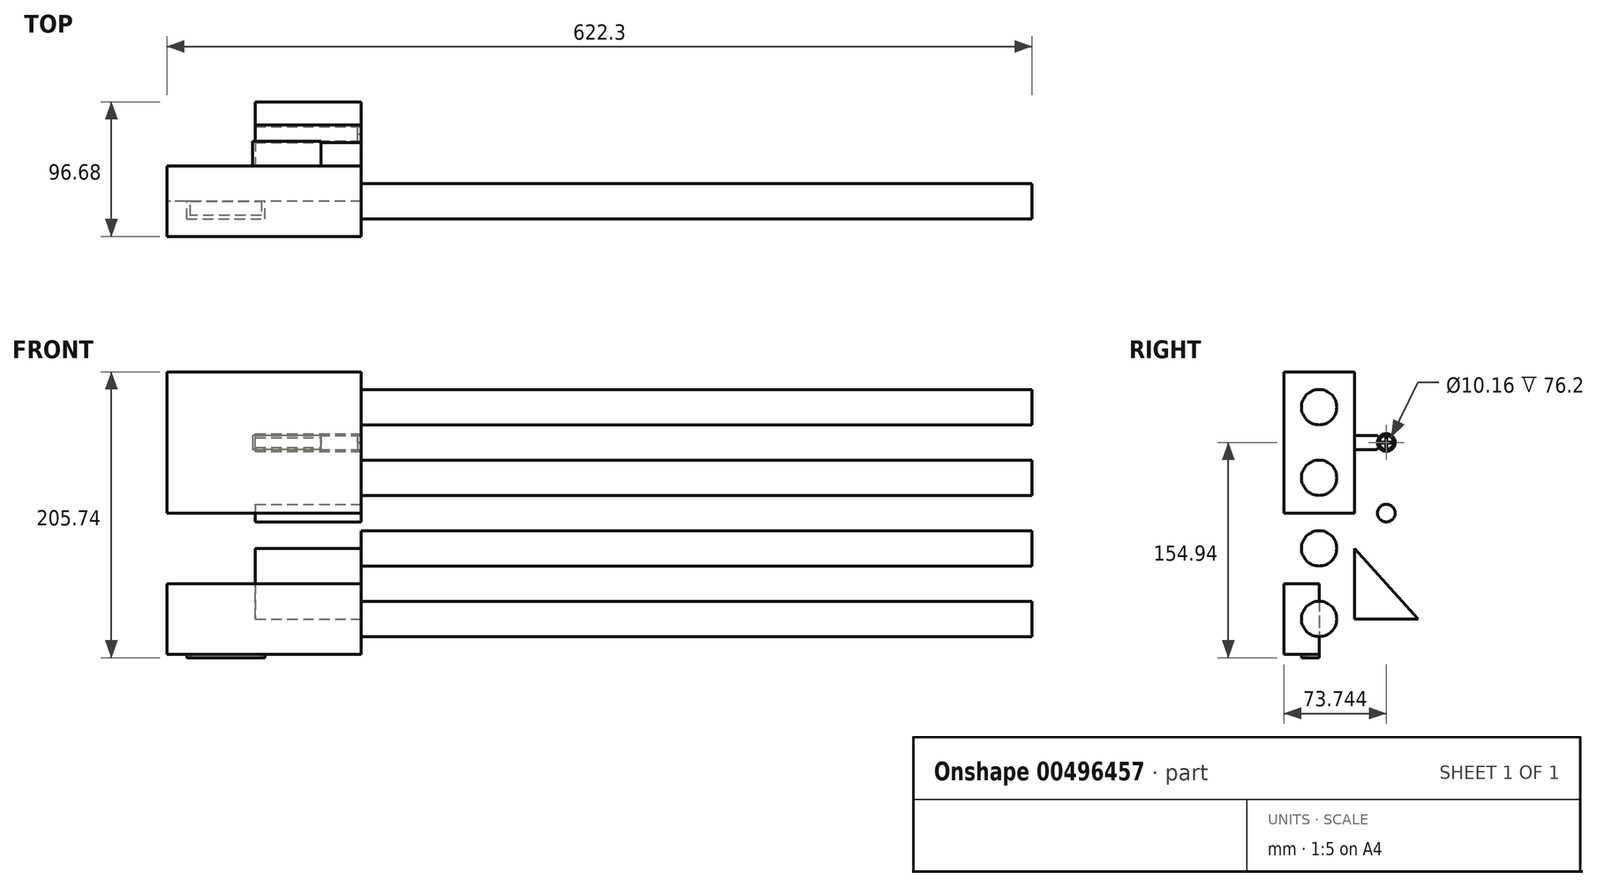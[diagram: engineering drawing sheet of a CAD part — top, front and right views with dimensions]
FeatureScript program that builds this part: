
annotation { "Feature Type Name" : "Feature", "Feature Type Description" : "" }
export const myFeature = defineFeature(function(context is Context, id is Id, definition is map)
    precondition{}
    {
        {
            var Q0;
            Q0=qCreatedBy(makeId("Top.planeOp"),FACE);
            var sketch = newSketch(context, id + "F0", { "sketchPlane" : qUnion([Q0])});
            skLineSegment(sketch, "E0.bottom", {"start": v(267.1, 70.34) * mm, "end": v(-139.3, 70.34) * mm});
            skLineSegment(sketch, "E0.top", {"start": v(267.1, 57.64) * mm, "end": v(-139.3, 57.64) * mm});
            skLineSegment(sketch, "E0.left", {"start": v(267.1, 70.34) * mm, "end": v(267.1, 57.64) * mm});
            skLineSegment(sketch, "E0.right", {"start": v(-139.3, 70.34) * mm, "end": v(-139.3, 57.64) * mm});
            skLineSegment(sketch, "E1.bottom", {"start": v(-139.3, 70.34) * mm, "end": v(-279, 70.34) * mm});
            skLineSegment(sketch, "E1.top", {"start": v(-139.3, 32.24) * mm, "end": v(-279, 32.24) * mm});
            skLineSegment(sketch, "E1.left", {"start": v(-139.3, 70.34) * mm, "end": v(-139.3, 32.24) * mm});
            skLineSegment(sketch, "E1.right", {"start": v(-279, 70.34) * mm, "end": v(-279, 32.24) * mm});
            skLineSegment(sketch, "E2.bottom", {"start": v(-279, 70.34) * mm, "end": v(-139.3, 70.34) * mm});
            skLineSegment(sketch, "E2.top", {"start": v(-279, 70.34) * mm, "end": v(-139.3, 70.34) * mm});
            skLineSegment(sketch, "E2.left", {"start": v(-279, 70.34) * mm, "end": v(-279, 70.34) * mm});
            skLineSegment(sketch, "E2.right", {"start": v(-139.3, 70.34) * mm, "end": v(-139.3, 70.34) * mm});
            skLineSegment(sketch, "E3.top", {"start": v(-279, 108.44) * mm, "end": v(-139.3, 108.44) * mm});
            skLineSegment(sketch, "E3.left", {"start": v(-279, 70.34) * mm, "end": v(-279, 108.44) * mm});
            skLineSegment(sketch, "E3.right", {"start": v(-139.3, 70.34) * mm, "end": v(-139.3, 108.44) * mm});
            skSolve(sketch);
        }
        {
            var Q0;
            {var subQ0=sQuery(id+"F0.wireOp",EDGE,"E0.bottom");Q0=makeQuery(id+"F0.imprint","IMPRINT",FACE,{"disambiguationData":[TD([[makeQuery(id+"F0.imprint","IMPRINT",EDGE,{"derivedFrom":subQ0}),1.0]])]});}
            var Q1;
            Q1=sQuery(id+"F0.wireOp",EDGE,"E0.bottom");
            revolve(context, id + "F1", {"entities" : qUnion([Q0]), "axis" : qUnion([Q1]), "revolveType" : RevolveType.FULL});
        }
        {
            var Q0;
            Q0=makeQuery(id+"F0.imprint","IMPRINT",FACE,{"disambiguationData":[TD([[makeQuery(id+"F0.imprint","IMPRINT",EDGE,{"derivedFrom":sQuery(id+"F0.wireOp",EDGE,"E2.bottom")}),1.0]])]});
            var Q1;
            {var subQ2=sQuery(id+"F0.wireOp",EDGE,"E1.top");Q1=makeQuery(id+"F0.imprint","IMPRINT",FACE,{"disambiguationData":[TD([[makeQuery(id+"F0.imprint","IMPRINT",EDGE,{"derivedFrom":subQ2}),-1.0]])]});}
            extrude(context, id + "F2", {"entities" : qUnion([Q0, Q1]), "operationType" : NewBodyOperationType.ADD, "depth" : 25.4 * mm});
        }
        {
            var Q0;
            Q0=makeQuery(id+"F0.imprint","IMPRINT",FACE,{"disambiguationData":[TD([[makeQuery(id+"F0.imprint","IMPRINT",EDGE,{"derivedFrom":sQuery(id+"F0.wireOp",EDGE,"E2.bottom")}),1.0]])]});
            var Q1;
            {var subQ2=sQuery(id+"F0.wireOp",EDGE,"E1.top");Q1=makeQuery(id+"F0.imprint","IMPRINT",FACE,{"disambiguationData":[TD([[makeQuery(id+"F0.imprint","IMPRINT",EDGE,{"derivedFrom":subQ2}),-1.0]])]});}
            extrude(context, id + "F3", {"entities" : qUnion([Q0, Q1]), "operationType" : NewBodyOperationType.ADD, "depth" : -25.4 * mm});
        }
        {
            var Q0;
            Q0=makeQuery(id+"F1.opRevolve","SWEPT_FACE",FACE,{"disambiguationData":[OSD([sQuery(id+"F0.wireOp",EDGE,"E0.left")])]});
            extrude(context, id + "F4", {"entities" : qUnion([Q0]), "operationType" : NewBodyOperationType.ADD, "depth" : 76.2 * mm});
        }
        {
            var Q0;
            {var subQ0=sQuery(id+"F0.wireOp",EDGE,"E3.right");var subQ1=sQuery(id+"F0.wireOp",EDGE,"E1.left");Q0=makeQuery(id+"F3.boolean.opBoolean","MERGE",FACE,{"derivedFrom":[makeQuery(id+"F2.opExtrude","SWEPT_FACE",FACE,{"disambiguationData":[OSD([subQ1,subQ0])]}),makeQuery(id+"F3.opExtrude","SWEPT_FACE",FACE,{"disambiguationData":[OSD([subQ1,subQ0])]})]});}
            var sketch = newSketch(context, id + "F5", { "sketchPlane" : qUnion([Q0])});
            skLineSegment(sketch, "E4", {"start": v(32.24, 25.4) * mm, "end": v(32.24, 76.2) * mm});
            skLineSegment(sketch, "E5", {"start": v(108.44, 25.4) * mm, "end": v(108.44, 76.2) * mm});
            skLineSegment(sketch, "E6", {"start": v(32.24, 76.2) * mm, "end": v(108.44, 76.2) * mm});
            skLineSegment(sketch, "E7", {"start": v(32.24, 76.2) * mm, "end": v(32.24, 127) * mm});
            skLineSegment(sketch, "E8", {"start": v(32.24, 127) * mm, "end": v(32.24, 177.8) * mm});
            skLineSegment(sketch, "E9", {"start": v(108.44, 76.2) * mm, "end": v(108.44, 127) * mm});
            skLineSegment(sketch, "E10", {"start": v(108.44, 127) * mm, "end": v(108.44, 177.8) * mm});
            skLineSegment(sketch, "E11", {"start": v(32.24, 127) * mm, "end": v(108.44, 127) * mm});
            skLineSegment(sketch, "E12", {"start": v(32.24, 177.8) * mm, "end": v(108.44, 177.8) * mm});
            skSolve(sketch);
        }
        {
            var Q0;
            Q0=makeQuery(id+"F5.imprint","IMPRINT",FACE,{"disambiguationData":[TD([[makeQuery(id+"F5.imprint","IMPRINT",EDGE,{"derivedFrom":sQuery(id+"F5.wireOp",EDGE,"E8")}),-1.0]])]});
            var Q1;
            Q1=makeQuery(id+"F5.imprint","IMPRINT",FACE,{"disambiguationData":[TD([[makeQuery(id+"F5.imprint","IMPRINT",EDGE,{"derivedFrom":sQuery(id+"F5.wireOp",EDGE,"E6")}),1.0]])]});
            var Q2;
            Q2=makeQuery(id+"F5.imprint","IMPRINT",FACE,{"disambiguationData":[TD([[makeQuery(id+"F5.imprint","IMPRINT",EDGE,{"derivedFrom":sQuery(id+"F5.wireOp",EDGE,"E4")}),-1.0]])]});
            extrude(context, id + "F6", {"entities" : qUnion([Q0, Q1, Q2]), "operationType" : NewBodyOperationType.ADD, "depth" : -139.7 * mm});
        }
        {
            var Q0;
            {var subQ0=sQuery(id+"F0.wireOp",EDGE,"E3.right");var subQ1=sQuery(id+"F0.wireOp",EDGE,"E1.left");Q0=makeQuery(id+"F6.boolean.opBoolean","MERGE",FACE,{"derivedFrom":[makeQuery(id+"F3.boolean.opBoolean","MERGE",FACE,{"derivedFrom":[makeQuery(id+"F2.opExtrude","SWEPT_FACE",FACE,{"disambiguationData":[OSD([subQ1,subQ0])]}),makeQuery(id+"F3.opExtrude","SWEPT_FACE",FACE,{"disambiguationData":[OSD([subQ1,subQ0])]})]}),makeQuery(id+"F6.opExtrude","CAP_FACE",FACE,{"disambiguationData":[OSD([subQ1,subQ0,sQuery(id+"F5.wireOp",EDGE,"E4"),sQuery(id+"F5.wireOp",EDGE,"E5"),sQuery(id+"F5.wireOp",EDGE,"E7"),sQuery(id+"F5.wireOp",EDGE,"E8"),sQuery(id+"F5.wireOp",EDGE,"E9"),sQuery(id+"F5.wireOp",EDGE,"E10"),sQuery(id+"F5.wireOp",EDGE,"E12")])],"isStart":true})]});}
            var sketch = newSketch(context, id + "F7", { "sketchPlane" : qUnion([Q0])});
            skCircle(sketch, "E13", {"center": v(70.34, 101.6) * mm, "radius": 12.7 * mm});
            skCircle(sketch, "E14", {"center": v(70.34, 152.4) * mm, "radius": 12.7 * mm});
            skCircle(sketch, "E15", {"center": v(70.34, 50.8) * mm, "radius": 12.7 * mm});
            skSolve(sketch);
        }
        {
            var Q0;
            Q0=makeQuery(id+"F7.imprint","IMPRINT",FACE,{"disambiguationData":[TD([[makeQuery(id+"F7.imprint","IMPRINT",EDGE,{"derivedFrom":sQuery(id+"F7.wireOp",EDGE,"E15")}),1.0]])]});
            var Q1;
            Q1=makeQuery(id+"F7.imprint","IMPRINT",FACE,{"disambiguationData":[TD([[makeQuery(id+"F7.imprint","IMPRINT",EDGE,{"derivedFrom":sQuery(id+"F7.wireOp",EDGE,"E13")}),1.0]])]});
            var Q2;
            Q2=makeQuery(id+"F7.imprint","IMPRINT",FACE,{"disambiguationData":[TD([[makeQuery(id+"F7.imprint","IMPRINT",EDGE,{"derivedFrom":sQuery(id+"F7.wireOp",EDGE,"E14")}),1.0]])]});
            extrude(context, id + "F8", {"entities" : qUnion([Q0, Q1, Q2]), "operationType" : NewBodyOperationType.ADD, "depth" : 482.6 * mm});
        }
        {
            var Q0;
            {var subQ0=sQuery(id+"F0.wireOp",EDGE,"E3.top");Q0=makeQuery(id+"F6.boolean.opBoolean","MERGE",FACE,{"derivedFrom":[makeQuery(id+"F3.boolean.opBoolean","MERGE",FACE,{"derivedFrom":[makeQuery(id+"F2.opExtrude","SWEPT_FACE",FACE,{"disambiguationData":[OSD([subQ0])]}),makeQuery(id+"F3.opExtrude","SWEPT_FACE",FACE,{"disambiguationData":[OSD([subQ0])]})]}),makeQuery(id+"F6.opExtrude","SWEPT_FACE",FACE,{"disambiguationData":[OSD([sQuery(id+"F5.wireOp",EDGE,"E5"),sQuery(id+"F5.wireOp",EDGE,"E9"),sQuery(id+"F5.wireOp",EDGE,"E10")])]})]});}
            extrude(context, id + "F9", {"entities" : qUnion([Q0]), "operationType" : NewBodyOperationType.ADD, "depth" : -7.62 * mm});
        }
        {
            var Q0;
            Q0=makeQuery(id+"F3.opExtrude","CAP_FACE",FACE,{"disambiguationData":[OSD([sQuery(id+"F0.wireOp",EDGE,"E1.top"),sQuery(id+"F0.wireOp",EDGE,"E1.left"),sQuery(id+"F0.wireOp",EDGE,"E1.right"),sQuery(id+"F0.wireOp",EDGE,"E3.top"),sQuery(id+"F0.wireOp",EDGE,"E3.left"),sQuery(id+"F0.wireOp",EDGE,"E3.right")])],"isStart":false});
            var sketch = newSketch(context, id + "F10", { "sketchPlane" : qUnion([Q0])});
            skLineSegment(sketch, "E16.bottom", {"start": v(-264.82, -57.64) * mm, "end": v(-208.52, -57.64) * mm});
            skLineSegment(sketch, "E16.top", {"start": v(-264.82, -83.04) * mm, "end": v(-208.52, -83.04) * mm});
            skLineSegment(sketch, "E16.left", {"start": v(-264.82, -57.64) * mm, "end": v(-264.82, -83.04) * mm});
            skLineSegment(sketch, "E16.right", {"start": v(-208.52, -57.64) * mm, "end": v(-208.52, -83.04) * mm});
            skSolve(sketch);
        }
        {
            var Q0;
            Q0=makeQuery(id+"F10.imprint","IMPRINT",FACE,{"disambiguationData":[TD([[makeQuery(id+"F10.imprint","IMPRINT",EDGE,{"derivedFrom":sQuery(id+"F10.wireOp",EDGE,"E16.bottom")}),-1.0]])]});
            extrude(context, id + "F11", {"entities" : qUnion([Q0]), "operationType" : NewBodyOperationType.ADD, "depth" : 2.54 * mm});
        }
        {
            var Q0;
            Q0=makeQuery(id+"F11.opExtrude","CAP_FACE",FACE,{"disambiguationData":[OSD([sQuery(id+"F10.wireOp",EDGE,"E16.bottom"),sQuery(id+"F10.wireOp",EDGE,"E16.top"),sQuery(id+"F10.wireOp",EDGE,"E16.left"),sQuery(id+"F10.wireOp",EDGE,"E16.right")])],"isStart":false});
            var sketch = newSketch(context, id + "F12", { "sketchPlane" : qUnion([Q0])});
            skLineSegment(sketch, "E17.0", {"start": v(-262.28, -60.18) * mm, "end": v(-262.28, -80.5) * mm});
            skLineSegment(sketch, "E17.1", {"start": v(-211.06, -60.18) * mm, "end": v(-262.28, -60.18) * mm});
            skLineSegment(sketch, "E17.2", {"start": v(-211.06, -80.5) * mm, "end": v(-211.06, -60.18) * mm});
            skLineSegment(sketch, "E17.3", {"start": v(-262.28, -80.5) * mm, "end": v(-211.06, -80.5) * mm});
            skSolve(sketch);
        }
        {
            var Q0;
            Q0=makeQuery(id+"F12.imprint","IMPRINT",FACE,{"disambiguationData":[TD([[makeQuery(id+"F12.imprint","IMPRINT",EDGE,{"derivedFrom":sQuery(id+"F12.wireOp",EDGE,"E17.0")}),1.0]])]});
            extrude(context, id + "F13", {"entities" : qUnion([Q0]), "operationType" : NewBodyOperationType.REMOVE, "oppositeDirection" : true, "depth" : 2.54 * mm});
        }
        {
            var Q0;
            {var subQ0=sQuery(id+"F0.wireOp",EDGE,"E3.top");Q0=makeQuery(id+"F6.boolean.opBoolean","MERGE",FACE,{"derivedFrom":[makeQuery(id+"F3.boolean.opBoolean","MERGE",FACE,{"derivedFrom":[makeQuery(id+"F2.opExtrude","SWEPT_FACE",FACE,{"disambiguationData":[OSD([subQ0])]}),makeQuery(id+"F3.opExtrude","SWEPT_FACE",FACE,{"disambiguationData":[OSD([subQ0])]})]}),makeQuery(id+"F6.opExtrude","SWEPT_FACE",FACE,{"disambiguationData":[OSD([sQuery(id+"F5.wireOp",EDGE,"E5"),sQuery(id+"F5.wireOp",EDGE,"E9"),sQuery(id+"F5.wireOp",EDGE,"E10")])]})]});}
            extrude(context, id + "F14", {"entities" : qUnion([Q0]), "operationType" : NewBodyOperationType.REMOVE, "oppositeDirection" : true, "depth" : 12.7 * mm});
        }
        {
            var Q0;
            {var subQ0=sQuery(id+"F0.wireOp",EDGE,"E1.top");Q0=makeQuery(id+"F6.boolean.opBoolean","MERGE",FACE,{"derivedFrom":[makeQuery(id+"F3.boolean.opBoolean","MERGE",FACE,{"derivedFrom":[makeQuery(id+"F2.opExtrude","SWEPT_FACE",FACE,{"disambiguationData":[OSD([subQ0])]}),makeQuery(id+"F3.opExtrude","SWEPT_FACE",FACE,{"disambiguationData":[OSD([subQ0])]})]}),makeQuery(id+"F6.opExtrude","SWEPT_FACE",FACE,{"disambiguationData":[OSD([sQuery(id+"F5.wireOp",EDGE,"E4"),sQuery(id+"F5.wireOp",EDGE,"E7"),sQuery(id+"F5.wireOp",EDGE,"E8")])]})]});}
            extrude(context, id + "F15", {"entities" : qUnion([Q0]), "operationType" : NewBodyOperationType.REMOVE, "oppositeDirection" : true, "depth" : 12.7 * mm});
        }
        {
            var Q0;
            {var subQ0=sQuery(id+"F0.wireOp",EDGE,"E3.right");var subQ1=sQuery(id+"F0.wireOp",EDGE,"E1.left");Q0=makeQuery(id+"F6.boolean.opBoolean","MERGE",FACE,{"derivedFrom":[makeQuery(id+"F3.boolean.opBoolean","MERGE",FACE,{"derivedFrom":[makeQuery(id+"F2.opExtrude","SWEPT_FACE",FACE,{"disambiguationData":[OSD([subQ1,subQ0])]}),makeQuery(id+"F3.opExtrude","SWEPT_FACE",FACE,{"disambiguationData":[OSD([subQ1,subQ0])]})]}),makeQuery(id+"F6.opExtrude","CAP_FACE",FACE,{"disambiguationData":[OSD([subQ1,subQ0,sQuery(id+"F5.wireOp",EDGE,"E4"),sQuery(id+"F5.wireOp",EDGE,"E5"),sQuery(id+"F5.wireOp",EDGE,"E7"),sQuery(id+"F5.wireOp",EDGE,"E8"),sQuery(id+"F5.wireOp",EDGE,"E9"),sQuery(id+"F5.wireOp",EDGE,"E10"),sQuery(id+"F5.wireOp",EDGE,"E12")])],"isStart":true})]});}
            var sketch = newSketch(context, id + "F16", { "sketchPlane" : qUnion([Q0])});
            skLineSegment(sketch, "E18", {"start": v(95.74, 177.8) * mm, "end": v(95.74, 152.4) * mm});
            skLineSegment(sketch, "E19", {"start": v(95.74, 152.4) * mm, "end": v(95.74, 101.6) * mm});
            skLineSegment(sketch, "E20", {"start": v(95.74, 101.6) * mm, "end": v(95.74, 50.8) * mm});
            skLineSegment(sketch, "E21", {"start": v(95.74, 50.8) * mm, "end": v(95.74, 0) * mm});
            skLineSegment(sketch, "E22", {"start": v(95.74, 152.4) * mm, "end": v(141.62, 152.4) * mm});
            skLineSegment(sketch, "E23", {"start": v(141.62, 152.4) * mm, "end": v(141.62, 0) * mm});
            skLineSegment(sketch, "E24", {"start": v(141.62, 0) * mm, "end": v(95.74, 0) * mm});
            skLineSegment(sketch, "E25", {"start": v(95.74, 101.6) * mm, "end": v(141.62, 101.6) * mm});
            skLineSegment(sketch, "E26", {"start": v(95.74, 50.8) * mm, "end": v(141.62, 50.8) * mm});
            skLineSegment(sketch, "E27", {"start": v(141.62, 50.8) * mm, "end": v(95.74, 0) * mm});
            skLineSegment(sketch, "E28", {"start": v(141.62, 0) * mm, "end": v(95.74, 50.8) * mm});
            skLineSegment(sketch, "E29", {"start": v(141.62, 50.8) * mm, "end": v(95.74, 101.6) * mm});
            skLineSegment(sketch, "E30", {"start": v(141.62, 101.6) * mm, "end": v(95.74, 152.4) * mm});
            skLineSegment(sketch, "E31", {"start": v(141.62, 152.4) * mm, "end": v(95.74, 101.6) * mm});
            skLineSegment(sketch, "E32", {"start": v(141.62, 101.6) * mm, "end": v(95.74, 50.8) * mm});
            skCircle(sketch, "E33", {"center": v(118.68, 25.4) * mm, "radius": 6.35 * mm});
            skCircle(sketch, "E34", {"center": v(118.68, 76.2) * mm, "radius": 6.35 * mm});
            skCircle(sketch, "E35", {"center": v(118.68, 127) * mm, "radius": 6.35 * mm});
            skSolve(sketch);
        }
        {
            var Q0;
            Q0=makeQuery(id+"F14.boolean.opBoolean","COPY",FACE,{"derivedFrom":makeQuery(id+"F14.opExtrude","CAP_FACE",FACE,{"disambiguationData":[OSD([sQuery(id+"F0.wireOp",EDGE,"E3.top"),sQuery(id+"F5.wireOp",EDGE,"E5"),sQuery(id+"F5.wireOp",EDGE,"E9"),sQuery(id+"F5.wireOp",EDGE,"E10")])],"isStart":false})});
            var sketch = newSketch(context, id + "F17", { "sketchPlane" : qUnion([Q0])});
            skLineSegment(sketch, "E36", {"start": v(139.3, -25.4) * mm, "end": v(139.3, 0) * mm});
            skLineSegment(sketch, "E37", {"start": v(139.3, 0) * mm, "end": v(139.3, 50.8) * mm});
            skLineSegment(sketch, "E38", {"start": v(139.3, 101.6) * mm, "end": v(139.3, 152.4) * mm});
            skLineSegment(sketch, "E39", {"start": v(139.3, 152.4) * mm, "end": v(279, 152.4) * mm});
            skLineSegment(sketch, "E40", {"start": v(139.3, 101.6) * mm, "end": v(279, 101.6) * mm});
            skLineSegment(sketch, "E41", {"start": v(139.3, 50.8) * mm, "end": v(279, 50.8) * mm});
            skLineSegment(sketch, "E42", {"start": v(139.3, 0) * mm, "end": v(279, 0) * mm});
            skLineSegment(sketch, "E43", {"start": v(145.8, 101.6) * mm, "end": v(145.8, 127) * mm});
            skLineSegment(sketch, "E44", {"start": v(145.8, 127) * mm, "end": v(279, 127) * mm});
            skLineSegment(sketch, "E45", {"start": v(168.22, 101.6) * mm, "end": v(168.22, 121.92) * mm});
            skLineSegment(sketch, "E46", {"start": v(235.75, 152.4) * mm, "end": v(235.75, 132.08) * mm});
            skLineSegment(sketch, "E47.bottom", {"start": v(168.22, 121.92) * mm, "end": v(235.75, 121.92) * mm});
            skLineSegment(sketch, "E47.top", {"start": v(168.22, 132.08) * mm, "end": v(235.75, 132.08) * mm});
            skLineSegment(sketch, "E48", {"start": v(217.4, 132.08) * mm, "end": v(217.4, 121.92) * mm});
            skLineSegment(sketch, "E49", {"start": v(168.22, 132.08) * mm, "end": v(168.22, 121.92) * mm});
            skLineSegment(sketch, "E50", {"start": v(169.07, 76.2) * mm, "end": v(224.04, 76.2) * mm});
            skSolve(sketch);
        }
        {
            var Q0;
            {var subQ0=sQuery(id+"F16.wireOp",EDGE,"E33");var subQ1=sQuery(id+"F16.wireOp",EDGE,"E27");var subQ2=makeQuery(id+"F16.imprint","INTERSECT",VERTEX,{"disambiguationData":[OD(0.0)],"derivedFrom":[subQ1,subQ0]});Q0=makeQuery(id+"F16.imprint","IMPRINT",FACE,{"disambiguationData":[TD([[makeQuery(id+"F16.imprint","IMPRINT",EDGE,{"disambiguationData":[TD([[subQ2,-1.0]])],"derivedFrom":subQ1}),1.0]])]});}
            var Q1;
            {var subQ0=sQuery(id+"F16.wireOp",EDGE,"E28");var subQ1=sQuery(id+"F16.wireOp",EDGE,"E27");var subQ2=makeQuery(id+"F16.imprint","INTERSECT",VERTEX,{"derivedFrom":[subQ1,subQ0]});Q1=makeQuery(id+"F16.imprint","IMPRINT",FACE,{"disambiguationData":[TD([[makeQuery(id+"F16.imprint","IMPRINT",EDGE,{"disambiguationData":[TD([[subQ2,-1.0]])],"derivedFrom":subQ1}),1.0]])]});}
            var Q2;
            {var subQ0=sQuery(id+"F16.wireOp",EDGE,"E28");var subQ1=sQuery(id+"F16.wireOp",EDGE,"E27");var subQ2=makeQuery(id+"F16.imprint","INTERSECT",VERTEX,{"derivedFrom":[subQ1,subQ0]});Q2=makeQuery(id+"F16.imprint","IMPRINT",FACE,{"disambiguationData":[TD([[makeQuery(id+"F16.imprint","IMPRINT",EDGE,{"disambiguationData":[TD([[subQ2,-1.0]])],"derivedFrom":subQ1}),-1.0]])]});}
            var Q3;
            {var subQ0=sQuery(id+"F16.wireOp",EDGE,"E33");var subQ1=sQuery(id+"F16.wireOp",EDGE,"E27");var subQ2=makeQuery(id+"F16.imprint","INTERSECT",VERTEX,{"disambiguationData":[OD(0.0)],"derivedFrom":[subQ1,subQ0]});Q3=makeQuery(id+"F16.imprint","IMPRINT",FACE,{"disambiguationData":[TD([[makeQuery(id+"F16.imprint","IMPRINT",EDGE,{"disambiguationData":[TD([[subQ2,-1.0]])],"derivedFrom":subQ1}),-1.0]])]});}
            var Q4;
            {var subQ0=sQuery(id+"F16.wireOp",EDGE,"E34");var subQ1=sQuery(id+"F16.wireOp",EDGE,"E29");var subQ2=makeQuery(id+"F16.imprint","INTERSECT",VERTEX,{"disambiguationData":[OD(0.0)],"derivedFrom":[subQ1,subQ0]});Q4=makeQuery(id+"F16.imprint","IMPRINT",FACE,{"disambiguationData":[TD([[makeQuery(id+"F16.imprint","IMPRINT",EDGE,{"disambiguationData":[TD([[subQ2,-1.0]])],"derivedFrom":subQ1}),-1.0]])]});}
            var Q5;
            {var subQ0=sQuery(id+"F16.wireOp",EDGE,"E34");var subQ1=sQuery(id+"F16.wireOp",EDGE,"E29");var subQ2=makeQuery(id+"F16.imprint","INTERSECT",VERTEX,{"disambiguationData":[OD(0.0)],"derivedFrom":[subQ1,subQ0]});Q5=makeQuery(id+"F16.imprint","IMPRINT",FACE,{"disambiguationData":[TD([[makeQuery(id+"F16.imprint","IMPRINT",EDGE,{"disambiguationData":[TD([[subQ2,-1.0]])],"derivedFrom":subQ1}),1.0]])]});}
            var Q6;
            {var subQ0=sQuery(id+"F16.wireOp",EDGE,"E32");var subQ1=sQuery(id+"F16.wireOp",EDGE,"E29");var subQ2=makeQuery(id+"F16.imprint","INTERSECT",VERTEX,{"derivedFrom":[subQ1,subQ0]});Q6=makeQuery(id+"F16.imprint","IMPRINT",FACE,{"disambiguationData":[TD([[makeQuery(id+"F16.imprint","IMPRINT",EDGE,{"disambiguationData":[TD([[subQ2,-1.0]])],"derivedFrom":subQ1}),1.0]])]});}
            var Q7;
            {var subQ0=sQuery(id+"F16.wireOp",EDGE,"E32");var subQ1=sQuery(id+"F16.wireOp",EDGE,"E29");var subQ2=makeQuery(id+"F16.imprint","INTERSECT",VERTEX,{"derivedFrom":[subQ1,subQ0]});Q7=makeQuery(id+"F16.imprint","IMPRINT",FACE,{"disambiguationData":[TD([[makeQuery(id+"F16.imprint","IMPRINT",EDGE,{"disambiguationData":[TD([[subQ2,-1.0]])],"derivedFrom":subQ1}),-1.0]])]});}
            var Q8;
            {var subQ0=sQuery(id+"F16.wireOp",EDGE,"E35");var subQ1=sQuery(id+"F16.wireOp",EDGE,"E30");var subQ2=makeQuery(id+"F16.imprint","INTERSECT",VERTEX,{"disambiguationData":[OD(0.0)],"derivedFrom":[subQ1,subQ0]});Q8=makeQuery(id+"F16.imprint","IMPRINT",FACE,{"disambiguationData":[TD([[makeQuery(id+"F16.imprint","IMPRINT",EDGE,{"disambiguationData":[TD([[subQ2,-1.0]])],"derivedFrom":subQ1}),-1.0]])]});}
            var Q9;
            {var subQ0=sQuery(id+"F16.wireOp",EDGE,"E35");var subQ1=sQuery(id+"F16.wireOp",EDGE,"E30");var subQ2=makeQuery(id+"F16.imprint","INTERSECT",VERTEX,{"disambiguationData":[OD(0.0)],"derivedFrom":[subQ1,subQ0]});Q9=makeQuery(id+"F16.imprint","IMPRINT",FACE,{"disambiguationData":[TD([[makeQuery(id+"F16.imprint","IMPRINT",EDGE,{"disambiguationData":[TD([[subQ2,-1.0]])],"derivedFrom":subQ1}),1.0]])]});}
            var Q10;
            {var subQ0=sQuery(id+"F16.wireOp",EDGE,"E31");var subQ1=sQuery(id+"F16.wireOp",EDGE,"E30");var subQ2=makeQuery(id+"F16.imprint","INTERSECT",VERTEX,{"derivedFrom":[subQ1,subQ0]});Q10=makeQuery(id+"F16.imprint","IMPRINT",FACE,{"disambiguationData":[TD([[makeQuery(id+"F16.imprint","IMPRINT",EDGE,{"disambiguationData":[TD([[subQ2,-1.0]])],"derivedFrom":subQ1}),1.0]])]});}
            var Q11;
            {var subQ0=sQuery(id+"F16.wireOp",EDGE,"E31");var subQ1=sQuery(id+"F16.wireOp",EDGE,"E30");var subQ2=makeQuery(id+"F16.imprint","INTERSECT",VERTEX,{"derivedFrom":[subQ1,subQ0]});Q11=makeQuery(id+"F16.imprint","IMPRINT",FACE,{"disambiguationData":[TD([[makeQuery(id+"F16.imprint","IMPRINT",EDGE,{"disambiguationData":[TD([[subQ2,-1.0]])],"derivedFrom":subQ1}),-1.0]])]});}
            extrude(context, id + "F18", {"entities" : qUnion([Q0, Q1, Q2, Q3, Q4, Q5, Q6, Q7, Q8, Q9, Q10, Q11]), "depth" : -76.2 * mm});
        }
        {
            var Q0;
            Q0=makeQuery(id+"F18.opExtrude","CAP_FACE",FACE,{"disambiguationData":[OSD([sQuery(id+"F16.wireOp",EDGE,"E35")])],"isStart":true});
            var sketch = newSketch(context, id + "F19", { "sketchPlane" : qUnion([Q0])});
            skLineSegment(sketch, "E51", {"start": v(113.44, 127.26) * mm, "end": v(125.03, 127.26) * mm});
            skLineSegment(sketch, "E52", {"start": v(113.44, 127.26) * mm, "end": v(112.34, 127.26) * mm});
            skLineSegment(sketch, "E53", {"start": v(113.44, 126.74) * mm, "end": v(112.34, 126.74) * mm});
            skLineSegment(sketch, "E54", {"start": v(113.44, 126.74) * mm, "end": v(125.03, 126.74) * mm});
            skLineSegment(sketch, "E55", {"start": v(118.4, 131.14) * mm, "end": v(118.4, 120.66) * mm});
            skLineSegment(sketch, "E56", {"start": v(118.4, 131.14) * mm, "end": v(118.4, 133.34) * mm});
            skLineSegment(sketch, "E57.MirrorCS", {"start": v(118.9, 131.14) * mm, "end": v(118.9, 133.34) * mm});
            skLineSegment(sketch, "E58.MirrorCS", {"start": v(118.9, 131.14) * mm, "end": v(118.9, 120.66) * mm});
            skCircle(sketch, "E59", {"center": v(118.68, 127) * mm, "radius": 5.08 * mm});
            skSolve(sketch);
        }
        {
            var Q0;
            {var subQ0=sQuery(id+"F19.wireOp",EDGE,"E59");var subQ1=sQuery(id+"F19.wireOp",EDGE,"E51");var subQ2=makeQuery(id+"F19.imprint","INTERSECT",VERTEX,{"disambiguationData":[OD(0.0)],"derivedFrom":[subQ1,subQ0]});Q0=makeQuery(id+"F19.imprint","IMPRINT",FACE,{"disambiguationData":[TD([[makeQuery(id+"F19.imprint","IMPRINT",EDGE,{"disambiguationData":[TD([[subQ2,-1.0]])],"derivedFrom":subQ1}),1.0]])]});}
            var Q1;
            {var subQ0=sQuery(id+"F19.wireOp",EDGE,"E59");var subQ1=sQuery(id+"F19.wireOp",EDGE,"E54");var subQ2=makeQuery(id+"F19.imprint","INTERSECT",VERTEX,{"disambiguationData":[OD(0.0)],"derivedFrom":[subQ1,subQ0]});Q1=makeQuery(id+"F19.imprint","IMPRINT",FACE,{"disambiguationData":[TD([[makeQuery(id+"F19.imprint","IMPRINT",EDGE,{"disambiguationData":[TD([[subQ2,-1.0]])],"derivedFrom":subQ1}),-1.0]])]});}
            var Q2;
            {var subQ0=sQuery(id+"F19.wireOp",EDGE,"E58.MirrorCS");var subQ1=sQuery(id+"F19.wireOp",EDGE,"E54");var subQ2=makeQuery(id+"F19.imprint","INTERSECT",VERTEX,{"derivedFrom":[subQ1,subQ0]});Q2=makeQuery(id+"F19.imprint","IMPRINT",FACE,{"disambiguationData":[TD([[makeQuery(id+"F19.imprint","IMPRINT",EDGE,{"disambiguationData":[TD([[subQ2,-1.0]])],"derivedFrom":subQ1}),-1.0]])]});}
            var Q3;
            {var subQ0=sQuery(id+"F19.wireOp",EDGE,"E58.MirrorCS");var subQ1=sQuery(id+"F19.wireOp",EDGE,"E51");var subQ2=makeQuery(id+"F19.imprint","INTERSECT",VERTEX,{"derivedFrom":[subQ1,subQ0]});Q3=makeQuery(id+"F19.imprint","IMPRINT",FACE,{"disambiguationData":[TD([[makeQuery(id+"F19.imprint","IMPRINT",EDGE,{"disambiguationData":[TD([[subQ2,-1.0]])],"derivedFrom":subQ1}),1.0]])]});}
            extrude(context, id + "F20", {"entities" : qUnion([Q0, Q1, Q2, Q3]), "operationType" : NewBodyOperationType.REMOVE, "oppositeDirection" : true, "depth" : 127 * mm});
        }
        {
            var Q0;
            {var subQ0=sQuery(id+"F19.wireOp",EDGE,"E55");var subQ1=sQuery(id+"F19.wireOp",EDGE,"E54");var subQ2=makeQuery(id+"F19.imprint","INTERSECT",VERTEX,{"derivedFrom":[subQ1,subQ0]});Q0=makeQuery(id+"F19.imprint","IMPRINT",FACE,{"disambiguationData":[TD([[makeQuery(id+"F19.imprint","IMPRINT",EDGE,{"disambiguationData":[TD([[subQ2,-1.0]])],"derivedFrom":subQ1}),-1.0]])]});}
            var Q1;
            {var subQ0=sQuery(id+"F19.wireOp",EDGE,"E59");var subQ1=sQuery(id+"F19.wireOp",EDGE,"E51");var subQ2=makeQuery(id+"F19.imprint","INTERSECT",VERTEX,{"disambiguationData":[OD(0.0)],"derivedFrom":[subQ1,subQ0]});Q1=makeQuery(id+"F19.imprint","IMPRINT",FACE,{"disambiguationData":[TD([[makeQuery(id+"F19.imprint","IMPRINT",EDGE,{"disambiguationData":[TD([[subQ2,-1.0]])],"derivedFrom":subQ1}),-1.0]])]});}
            var Q2;
            {var subQ6=sQuery(id+"F19.wireOp",EDGE,"E55");var subQ9=sQuery(id+"F19.wireOp",EDGE,"E51");var subQ10=makeQuery(id+"F19.imprint","INTERSECT",VERTEX,{"derivedFrom":[subQ9,subQ6]});Q2=makeQuery(id+"F19.imprint","IMPRINT",FACE,{"disambiguationData":[TD([[makeQuery(id+"F19.imprint","IMPRINT",EDGE,{"disambiguationData":[TD([[subQ10,-1.0]])],"derivedFrom":subQ9}),1.0]])]});}
            var Q3;
            {var subQ0=sQuery(id+"F19.wireOp",EDGE,"E58.MirrorCS");var subQ1=sQuery(id+"F19.wireOp",EDGE,"E51");var subQ2=makeQuery(id+"F19.imprint","INTERSECT",VERTEX,{"derivedFrom":[subQ1,subQ0]});Q3=makeQuery(id+"F19.imprint","IMPRINT",FACE,{"disambiguationData":[TD([[makeQuery(id+"F19.imprint","IMPRINT",EDGE,{"disambiguationData":[TD([[subQ2,-1.0]])],"derivedFrom":subQ1}),-1.0]])]});}
            var Q4;
            {var subQ0=sQuery(id+"F19.wireOp",EDGE,"E55");var subQ1=sQuery(id+"F19.wireOp",EDGE,"E51");var subQ2=makeQuery(id+"F19.imprint","INTERSECT",VERTEX,{"derivedFrom":[subQ1,subQ0]});Q4=makeQuery(id+"F19.imprint","IMPRINT",FACE,{"disambiguationData":[TD([[makeQuery(id+"F19.imprint","IMPRINT",EDGE,{"disambiguationData":[TD([[subQ2,-1.0]])],"derivedFrom":subQ1}),-1.0]])]});}
            extrude(context, id + "F21", {"entities" : qUnion([Q0, Q1, Q2, Q3, Q4]), "operationType" : NewBodyOperationType.REMOVE, "oppositeDirection" : true, "depth" : 101.6 * mm});
        }
        {
            var Q0;
            {var subQ0=sQuery(id+"F19.wireOp",EDGE,"E59");var subQ1=sQuery(id+"F19.wireOp",EDGE,"E51");var subQ2=makeQuery(id+"F19.imprint","INTERSECT",VERTEX,{"disambiguationData":[OD(0.0)],"derivedFrom":[subQ1,subQ0]});Q0=makeQuery(id+"F19.imprint","IMPRINT",FACE,{"disambiguationData":[TD([[makeQuery(id+"F19.imprint","IMPRINT",EDGE,{"disambiguationData":[TD([[subQ2,-1.0]])],"derivedFrom":subQ1}),-1.0]])]});}
            var Q1;
            {var subQ6=sQuery(id+"F19.wireOp",EDGE,"E55");var subQ9=sQuery(id+"F19.wireOp",EDGE,"E51");var subQ10=makeQuery(id+"F19.imprint","INTERSECT",VERTEX,{"derivedFrom":[subQ9,subQ6]});Q1=makeQuery(id+"F19.imprint","IMPRINT",FACE,{"disambiguationData":[TD([[makeQuery(id+"F19.imprint","IMPRINT",EDGE,{"disambiguationData":[TD([[subQ10,-1.0]])],"derivedFrom":subQ9}),1.0]])]});}
            var Q2;
            {var subQ0=sQuery(id+"F19.wireOp",EDGE,"E55");var subQ1=sQuery(id+"F19.wireOp",EDGE,"E54");var subQ2=makeQuery(id+"F19.imprint","INTERSECT",VERTEX,{"derivedFrom":[subQ1,subQ0]});Q2=makeQuery(id+"F19.imprint","IMPRINT",FACE,{"disambiguationData":[TD([[makeQuery(id+"F19.imprint","IMPRINT",EDGE,{"disambiguationData":[TD([[subQ2,-1.0]])],"derivedFrom":subQ1}),-1.0]])]});}
            var Q3;
            {var subQ0=sQuery(id+"F19.wireOp",EDGE,"E58.MirrorCS");var subQ1=sQuery(id+"F19.wireOp",EDGE,"E51");var subQ2=makeQuery(id+"F19.imprint","INTERSECT",VERTEX,{"derivedFrom":[subQ1,subQ0]});Q3=makeQuery(id+"F19.imprint","IMPRINT",FACE,{"disambiguationData":[TD([[makeQuery(id+"F19.imprint","IMPRINT",EDGE,{"disambiguationData":[TD([[subQ2,-1.0]])],"derivedFrom":subQ1}),-1.0]])]});}
            var Q4;
            {var subQ0=sQuery(id+"F19.wireOp",EDGE,"E55");var subQ1=sQuery(id+"F19.wireOp",EDGE,"E51");var subQ2=makeQuery(id+"F19.imprint","INTERSECT",VERTEX,{"derivedFrom":[subQ1,subQ0]});Q4=makeQuery(id+"F19.imprint","IMPRINT",FACE,{"disambiguationData":[TD([[makeQuery(id+"F19.imprint","IMPRINT",EDGE,{"disambiguationData":[TD([[subQ2,-1.0]])],"derivedFrom":subQ1}),-1.0]])]});}
            extrude(context, id + "F22", {"entities" : qUnion([Q0, Q1, Q2, Q3, Q4]), "operationType" : NewBodyOperationType.ADD, "depth" : -2.54 * mm});
        }
        {
            var Q0;
            {var subQ0=sQuery(id+"F17.wireOp",EDGE,"E49");var subQ1=sQuery(id+"F17.wireOp",EDGE,"E44");var subQ2=makeQuery(id+"F17.imprint","INTERSECT",VERTEX,{"derivedFrom":[subQ1,subQ0]});Q0=makeQuery(id+"F17.imprint","IMPRINT",FACE,{"disambiguationData":[TD([[makeQuery(id+"F17.imprint","IMPRINT",EDGE,{"disambiguationData":[TD([[subQ2,-1.0]])],"derivedFrom":subQ1}),-1.0]])]});}
            var Q1;
            {var subQ0=sQuery(id+"F17.wireOp",EDGE,"E49");var subQ1=sQuery(id+"F17.wireOp",EDGE,"E44");var subQ2=makeQuery(id+"F17.imprint","INTERSECT",VERTEX,{"derivedFrom":[subQ1,subQ0]});Q1=makeQuery(id+"F17.imprint","IMPRINT",FACE,{"disambiguationData":[TD([[makeQuery(id+"F17.imprint","IMPRINT",EDGE,{"disambiguationData":[TD([[subQ2,-1.0]])],"derivedFrom":subQ1}),1.0]])]});}
            extrude(context, id + "F23", {"entities" : qUnion([Q0, Q1]), "operationType" : NewBodyOperationType.ADD, "depth" : 17.78 * mm, "offsetDistance" : 25.4 * mm});
        }
        {
            var Q0;
            Q0=makeQuery(id+"F23.opExtrude","CAP_EDGE",EDGE,{"disambiguationData":[OSD([sQuery(id+"F17.wireOp",EDGE,"E47.bottom")])],"isStart":false});
            fillet(context, id + "F24", {"entities" : qUnion([Q0]), "radius" : 2.54 * mm, "tangentPropagation" : true, "allowEdgeOverflow" : false});
        }
        {
            var Q0;
            Q0=makeQuery(id+"F23.opExtrude","CAP_EDGE",EDGE,{"disambiguationData":[OSD([sQuery(id+"F17.wireOp",EDGE,"E47.top")])],"isStart":false});
            fillet(context, id + "F25", {"entities" : qUnion([Q0]), "radius" : 2.54 * mm, "tangentPropagation" : true, "allowEdgeOverflow" : false});
        }
    });
